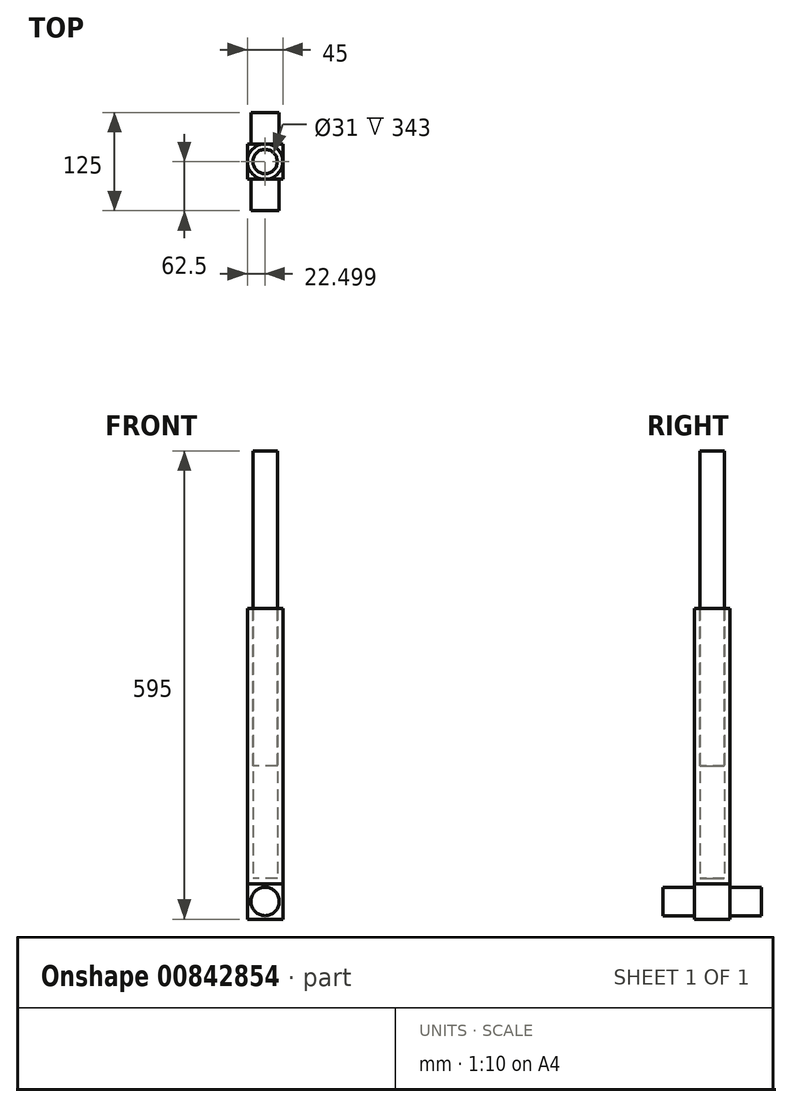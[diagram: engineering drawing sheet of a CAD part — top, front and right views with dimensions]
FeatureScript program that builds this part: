
annotation { "Feature Type Name" : "Feature", "Feature Type Description" : "" }
export const myFeature = defineFeature(function(context is Context, id is Id, definition is map)
    precondition{}
    {
        {
            var Q0;
            Q0=qCreatedBy(makeId("Top.planeOp"),FACE);
            var sketch = newSketch(context, id + "F0", { "sketchPlane" : qUnion([Q0])});
            skCircle(sketch, "E0", {"center": v(41.04, 0) * mm, "radius": 22.5 * mm});
            skSolve(sketch);
        }
        {
            var Q0;
            Q0=makeQuery(id+"F0.imprint","IMPRINT",FACE,{"disambiguationData":[TD([[makeQuery(id+"F0.imprint","IMPRINT",EDGE,{"derivedFrom":sQuery(id+"F0.wireOp",EDGE,"E0")}),1.0]])]});
            var Q1;
            Q1=sQuery(id+"F0.wireOp",EDGE,"E0");
            extrude(context, id + "F1", {"entities" : qUnion([Q0]), "surfaceEntities" : qUnion([Q1]), "depth" : 350 * mm, "offsetDistance" : 25 * mm});
        }
        {
            var Q0;
            Q0=makeQuery(id+"F1.opExtrude","CAP_FACE",FACE,{"disambiguationData":[OSD([sQuery(id+"F0.wireOp",EDGE,"E0")])],"isStart":false});
            shell(context, id + "F2", {"entities" : qUnion([Q0]), "thickness" : 7 * mm});
        }
        {
            var Q0;
            Q0=makeQuery(id+"F1.opExtrude","CAP_FACE",FACE,{"disambiguationData":[OSD([sQuery(id+"F0.wireOp",EDGE,"E0")])],"isStart":false});
            var sketch = newSketch(context, id + "F3", { "sketchPlane" : qUnion([Q0])});
            skCircle(sketch, "E1", {"center": v(41.04, 0) * mm, "radius": 15.5 * mm});
            skSolve(sketch);
        }
        {
            var Q0;
            Q0 = qSketchRegion(id + "F3", true);
            extrude(context, id + "F4", {"entities" : qUnion([Q0]), "endBound" : BoundingType.SYMMETRIC, "oppositeDirection" : true, "depth" : 400 * mm, "offsetDistance" : 25 * mm});
        }
        {
            var Q0;
            Q0=makeQuery(id+"F1.opExtrude","CAP_FACE",FACE,{"disambiguationData":[OSD([sQuery(id+"F0.wireOp",EDGE,"E0")])],"isStart":true});
            var sketch = newSketch(context, id + "F5", { "sketchPlane" : qUnion([Q0])});
            skLineSegment(sketch, "E2.bottom", {"start": v(18.54, 22.5) * mm, "end": v(63.54, 22.5) * mm});
            skLineSegment(sketch, "E2.top", {"start": v(18.54, -22.5) * mm, "end": v(63.54, -22.5) * mm});
            skLineSegment(sketch, "E2.left", {"start": v(18.54, 22.5) * mm, "end": v(18.54, -22.5) * mm});
            skLineSegment(sketch, "E2.right", {"start": v(63.54, 22.5) * mm, "end": v(63.54, -22.5) * mm});
            skPoint(sketch, "E2.middle", {"position": v(41.04, 0) * mm});
            skSolve(sketch);
        }
        {
            var Q0;
            Q0 = qSketchRegion(id + "F5", true);
            extrude(context, id + "F6", {"entities" : qUnion([Q0]), "operationType" : NewBodyOperationType.ADD, "depth" : 45 * mm, "offsetDistance" : 25 * mm});
        }
        {
            var Q0;
            Q0=qCreatedBy(makeId("Front.planeOp"),FACE);
            var sketch = newSketch(context, id + "F7", { "sketchPlane" : qUnion([Q0])});
            skCircle(sketch, "E3", {"center": v(41.04, -22.5) * mm, "radius": 18 * mm});
            skSolve(sketch);
        }
        {
            var Q0;
            Q0 = qSketchRegion(id + "F7", true);
            var Q1;
            Q1=sQuery(id+"F7.wireOp",EDGE,"E3");
            extrude(context, id + "F8", {"entities" : qUnion([Q0]), "operationType" : NewBodyOperationType.ADD, "surfaceEntities" : qUnion([Q1]), "endBound" : BoundingType.SYMMETRIC, "oppositeDirection" : true, "depth" : 125 * mm, "offsetDistance" : 25 * mm});
        }
    });
